# Revit family: Desks-Preconfigured-Teknion-B_SCBS_Convex_Desk_with_Single_Pedestal-R2019
name_source: partatom
category: Furniture
units: mm (PartAtom-declared; Revit-internal decimal feet)

## family parameters
Always vertical = Yes
Cut with Voids When Loaded = No
OmniClass Number = 23.40.20.00
OmniClass Title = General Furniture and Specialties
Room Calculation Point = No
Shared = Yes
Work Plane-Based = No

## types (5) — shared parameters
Assembly Code = E2020200
Manufacturer = Teknion
Manufacturer Fax = 416.661.4586
Part Number = B_SCBS
Product Documentation Link = https://www.teknion.com
Product Line = Expansion Casegoods
Product Page URL = https://www.teknion.com
Series = Expansion Casegoods
Storage Configuration Note = Please choose one of the following options below.
Sustainability Data = https://www.teknion.com
URL = www.teknion.com
Unit Weight URL = http://www.teknion.com
Warranty = http://www.teknion.com

## per-type parameters (varying)
| type | Depth | Description | Elliptical Grommet Offset | Model | Raidus Offset | Rectangular Grommet Offset | Worksurface Thickness |
| 1-3/16" Thick WS, 36" Depth | 36 " | Convex Desk with Single Pedestal, 1-3/16" Worksurface Thickness, 36" Depth | 2.209 " | BMSCBS36____ | 11 " | 8.803 " | 1.189 " |
| 1-3/16" Thick WS, 30" Depth | 30 " | Convex Desk with Single Pedestal, 1-3/16" Worksurface Thickness, 30" Depth | 3.24 " | BMSCBS30____ | 7.981 " | 6.834 " | 1.189 " |
| 1" Thick WS, 30" Depth | 30 " | Convex Desk with Single Pedestal, 1" Worksurface Thickness, 30" Depth | 3.24 " | BDSCBS30____ | 7.981 " | 6.834 " | 1.016 " |
| 1-9/16" Thick WS, 36" Depth | 36 " | Convex Desk with Single Pedestal, 1-9/16" Worksurface Thickness, 36" Depth | 2.209 " | BXSCBS36____ | 11 " | 8.803 " | 1.555 " |
| 1-9/16" Thick WS, 30" Depth | 30 " | Convex Desk with Single Pedestal, 1-9/16" Worksurface Thickness, 30" Depth | 3.24 " | BXSCBS30____ | 7.981 " | 6.834 " | 1.555 " |

## geometry (parser evidence)
native form markers: Sweep x2
no freeform markers — native parametric forms only
